# Revit family: Reece_Toilet_American Standard_Signature_Wall Hung_Back Inlet_With E Bidet
name_source: partatom
category: Plumbing Fixtures
revit_build: Autodesk Revit 2018 (Build: 20190510_1515(x64)
units: mm (PartAtom-declared; Revit-internal decimal feet)

## family parameters
Always vertical = Yes
Cut with Voids When Loaded = No
Part Type = Normal
Room Calculation Point = No
Round Connector Dimension = Use Diameter
Shared = No
Work Plane-Based = No

## types (1)
- Soft Close_White
    Description = American Standard Signature Hygiene Rim Wall Hung Pan with SpaLet E-Bidet Seat (4 Star)
    Disclaimer = THIS FILE IS THE PROPERTY OF THE REECE GROUP. IT MAY NOT BE REPRODUCED, REVERSE-ENGINEERED OR MODIFIED. ANY REPUBLICATION, TRANSMISSION OR DISTRIBUTION FOR THE PURPOSE OF COMMERCIALLY EXPLOITING THE FILES IS PROHIBITED.
    Keynote = Product #1805216, Reece_Toilet_American Standard_Signature_Wall Hung_Back Inlet_With E Bidet - Soft Close_White
    Manufacturer = American Standard
    Model = Signature
    Reece_Back_Inlet = 55 mm  [stored 0.180446 ft]
    Reece_Detail_Additional = SpaLet E-Bidet Seat
    Reece_Detail_Connector = Back Inlet
    Reece_Detail_Disclaimer = THIS FILE IS THE PROPERTY OF THE REECE GROUP. IT MAY NOT BE REPRODUCED, REVERSE-ENGINEERED OR MODIFIED. ANY REPUBLICATION, TRANSMISSION OR DISTRIBUTION FOR THE PURPOSE OF COMMERCIALLY EXPLOITING THE FILES IS PROHIBITED.
    Reece_Detail_Function = P Trap
    Reece_Detail_Installation = Wall Hung
    Reece_E Bidet_Inlet = 12 mm  [stored 0.0393701 ft]
    Reece_Material_Main = Reece_Vitreous China_White
    Reece_Material_Seat = Reece_Plastic_White
    Reece_Material_Secondary = Reece_Brass_Chrome
    Reece_Overall_Height = 415 mm  [stored 1.36155 ft]
    Reece_Overall_Projection = 550 mm
    Reece_Overall_Width = 381 mm  [stored 1.25 ft]
    Reece_P_Trap = 102 mm
    Reece_Pan_Height = 290 mm  [stored 0.951444 ft]
    Reece_Product_Brand = American Standard
    Reece_Product_Description = American Standard Signature Hygiene Rim Wall Hung Pan with SpaLet E-Bidet Seat (4 Star)
    Reece_Product_Mount = Floor Mounted
    Reece_Product_Number = 1805216
    Reece_Product_Sub Brand = Signature
    Reece_Product_Type = Toilet
    Reece_Product_Web Page = https://www.reece.com.au
    Type Comments = Toilet
    URL = https://www.reece.com.au

note: [stored X ft] marks values corroborated as IEEE doubles in the binary element streams (Revit-internal decimal feet)

## geometry (parser evidence)
native form markers: Sweep x7
no freeform markers — native parametric forms only
